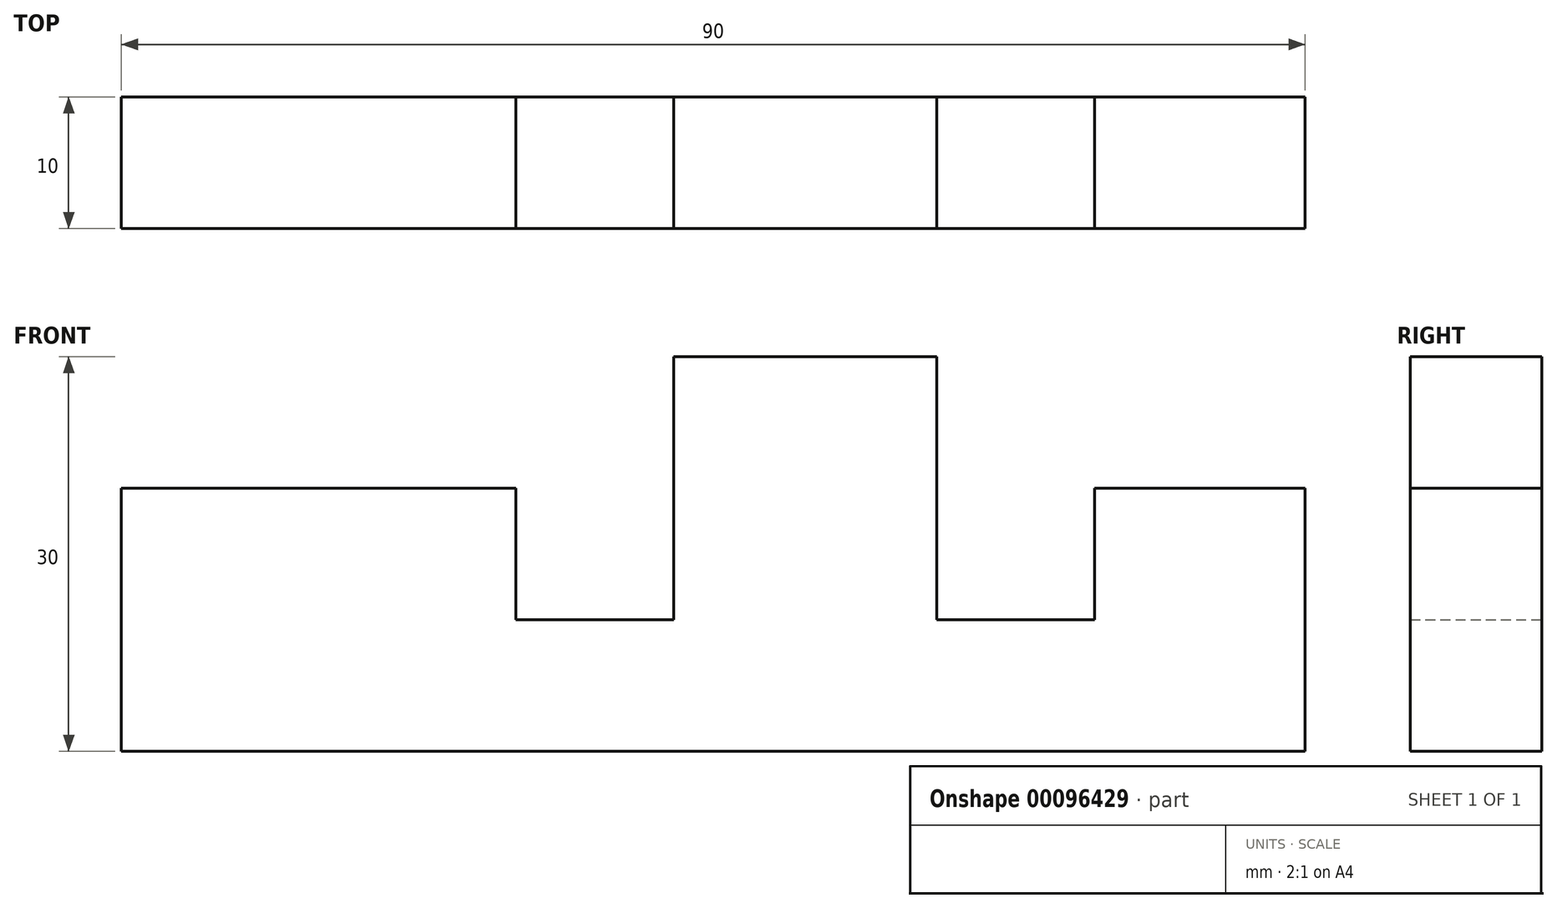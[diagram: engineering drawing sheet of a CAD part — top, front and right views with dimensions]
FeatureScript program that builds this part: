
annotation { "Feature Type Name" : "Feature", "Feature Type Description" : "" }
export const myFeature = defineFeature(function(context is Context, id is Id, definition is map)
    precondition{}
    {
        {
            var Q0;
            Q0=qCreatedBy(makeId("Front.planeOp"),FACE);
            var sketch = newSketch(context, id + "F0", { "sketchPlane" : qUnion([Q0])});
            skLineSegment(sketch, "E0", {"start": v(0, 0) * mm, "end": v(0, 20) * mm});
            skLineSegment(sketch, "E1", {"start": v(0, 0) * mm, "end": v(90, 0) * mm});
            skLineSegment(sketch, "E2", {"start": v(90, 0) * mm, "end": v(90, 20) * mm});
            skLineSegment(sketch, "E3", {"start": v(90, 20) * mm, "end": v(74, 20) * mm});
            skLineSegment(sketch, "E4", {"start": v(74, 20) * mm, "end": v(74, 10) * mm});
            skLineSegment(sketch, "E5", {"start": v(74, 10) * mm, "end": v(62, 10) * mm});
            skLineSegment(sketch, "E6", {"start": v(62, 10) * mm, "end": v(62, 30) * mm});
            skLineSegment(sketch, "E7", {"start": v(62, 30) * mm, "end": v(42, 30) * mm});
            skLineSegment(sketch, "E8", {"start": v(42, 30) * mm, "end": v(42, 10) * mm});
            skLineSegment(sketch, "E9", {"start": v(42, 10) * mm, "end": v(30, 10) * mm});
            skLineSegment(sketch, "E10", {"start": v(30, 10) * mm, "end": v(30, 20) * mm});
            skLineSegment(sketch, "E11", {"start": v(30, 20) * mm, "end": v(0, 20) * mm});
            skSolve(sketch);
        }
        {
            var Q0;
            Q0=makeQuery(id+"F0.imprint","IMPRINT",FACE,{"disambiguationData":[TD([[makeQuery(id+"F0.imprint","IMPRINT",EDGE,{"derivedFrom":sQuery(id+"F0.wireOp",EDGE,"E0")}),-1.0]])]});
            extrude(context, id + "F1", {"entities" : qUnion([Q0]), "depth" : 10 * mm});
        }
    });
